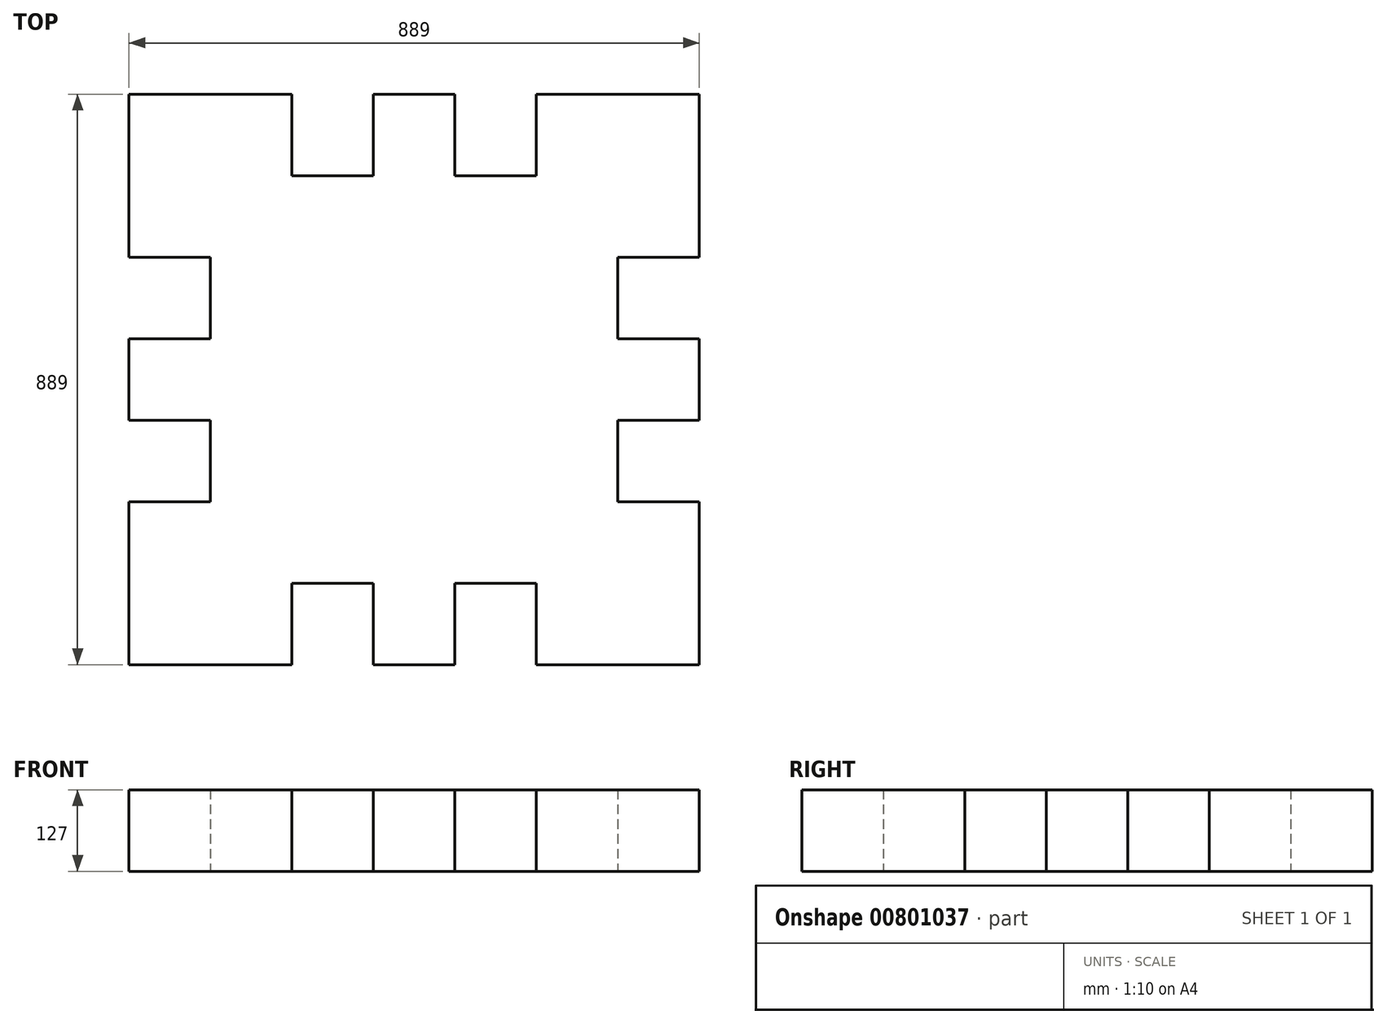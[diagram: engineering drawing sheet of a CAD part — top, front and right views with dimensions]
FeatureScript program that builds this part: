
annotation { "Feature Type Name" : "Feature", "Feature Type Description" : "" }
export const myFeature = defineFeature(function(context is Context, id is Id, definition is map)
    precondition{}
    {
        {
            var Q0;
            Q0=qCreatedBy(makeId("Top.planeOp"),FACE);
            var sketch = newSketch(context, id + "F0", { "sketchPlane" : qUnion([Q0])});
            skLineSegment(sketch, "E0.bottom", {"start": v(0, 0) * mm, "end": v(635, 0) * mm});
            skLineSegment(sketch, "E0.top", {"start": v(0, -635) * mm, "end": v(635, -635) * mm});
            skLineSegment(sketch, "E0.left", {"start": v(0, 0) * mm, "end": v(0, -635) * mm});
            skLineSegment(sketch, "E0.right", {"start": v(635, 0) * mm, "end": v(635, -635) * mm});
            skLineSegment(sketch, "E1.bottom", {"start": v(0, 0) * mm, "end": v(127, 0) * mm});
            skLineSegment(sketch, "E1.top", {"start": v(0, 127) * mm, "end": v(127, 127) * mm});
            skLineSegment(sketch, "E1.left", {"start": v(0, 0) * mm, "end": v(0, 127) * mm});
            skLineSegment(sketch, "E1.right", {"start": v(127, 0) * mm, "end": v(127, 127) * mm});
            skLineSegment(sketch, "E2.bottom", {"start": v(254, 0) * mm, "end": v(381, 0) * mm});
            skLineSegment(sketch, "E2.top", {"start": v(254, 127) * mm, "end": v(381, 127) * mm});
            skLineSegment(sketch, "E2.left", {"start": v(254, 0) * mm, "end": v(254, 127) * mm});
            skLineSegment(sketch, "E2.right", {"start": v(381, 0) * mm, "end": v(381, 127) * mm});
            skLineSegment(sketch, "E3.bottom", {"start": v(635, 0) * mm, "end": v(508, 0) * mm});
            skLineSegment(sketch, "E3.top", {"start": v(635, 127) * mm, "end": v(508, 127) * mm});
            skLineSegment(sketch, "E3.left", {"start": v(635, 0) * mm, "end": v(635, 127) * mm});
            skLineSegment(sketch, "E3.right", {"start": v(508, 0) * mm, "end": v(508, 127) * mm});
            skLineSegment(sketch, "E4.bottom", {"start": v(635, 0) * mm, "end": v(762, 0) * mm});
            skLineSegment(sketch, "E4.top", {"start": v(635, -127) * mm, "end": v(762, -127) * mm});
            skLineSegment(sketch, "E4.left", {"start": v(635, 0) * mm, "end": v(635, -127) * mm});
            skLineSegment(sketch, "E4.right", {"start": v(762, 0) * mm, "end": v(762, -127) * mm});
            skLineSegment(sketch, "E5.bottom", {"start": v(635, -254) * mm, "end": v(762, -254) * mm});
            skLineSegment(sketch, "E5.top", {"start": v(635, -381) * mm, "end": v(762, -381) * mm});
            skLineSegment(sketch, "E5.left", {"start": v(635, -254) * mm, "end": v(635, -381) * mm});
            skLineSegment(sketch, "E5.right", {"start": v(762, -254) * mm, "end": v(762, -381) * mm});
            skLineSegment(sketch, "E6.bottom", {"start": v(635, -635) * mm, "end": v(762, -635) * mm});
            skLineSegment(sketch, "E6.top", {"start": v(635, -508) * mm, "end": v(762, -508) * mm});
            skLineSegment(sketch, "E6.left", {"start": v(635, -635) * mm, "end": v(635, -508) * mm});
            skLineSegment(sketch, "E6.right", {"start": v(762, -635) * mm, "end": v(762, -508) * mm});
            skLineSegment(sketch, "E7.bottom", {"start": v(0, -635) * mm, "end": v(127, -635) * mm});
            skLineSegment(sketch, "E7.top", {"start": v(0, -762) * mm, "end": v(127, -762) * mm});
            skLineSegment(sketch, "E7.left", {"start": v(0, -635) * mm, "end": v(0, -762) * mm});
            skLineSegment(sketch, "E7.right", {"start": v(127, -635) * mm, "end": v(127, -762) * mm});
            skLineSegment(sketch, "E8.bottom", {"start": v(254, -635) * mm, "end": v(381, -635) * mm});
            skLineSegment(sketch, "E8.top", {"start": v(254, -762) * mm, "end": v(381, -762) * mm});
            skLineSegment(sketch, "E8.left", {"start": v(254, -635) * mm, "end": v(254, -762) * mm});
            skLineSegment(sketch, "E8.right", {"start": v(381, -635) * mm, "end": v(381, -762) * mm});
            skLineSegment(sketch, "E9.bottom", {"start": v(635, -635) * mm, "end": v(508, -635) * mm});
            skLineSegment(sketch, "E9.top", {"start": v(635, -762) * mm, "end": v(508, -762) * mm});
            skLineSegment(sketch, "E9.left", {"start": v(635, -635) * mm, "end": v(635, -762) * mm});
            skLineSegment(sketch, "E9.right", {"start": v(508, -635) * mm, "end": v(508, -762) * mm});
            skLineSegment(sketch, "E10.bottom", {"start": v(0, 0) * mm, "end": v(-127, 0) * mm});
            skLineSegment(sketch, "E10.top", {"start": v(0, -127) * mm, "end": v(-127, -127) * mm});
            skLineSegment(sketch, "E10.left", {"start": v(0, 0) * mm, "end": v(0, -127) * mm});
            skLineSegment(sketch, "E10.right", {"start": v(-127, 0) * mm, "end": v(-127, -127) * mm});
            skLineSegment(sketch, "E11.bottom", {"start": v(0, -635) * mm, "end": v(-127, -635) * mm});
            skLineSegment(sketch, "E11.top", {"start": v(0, -508) * mm, "end": v(-127, -508) * mm});
            skLineSegment(sketch, "E11.left", {"start": v(0, -635) * mm, "end": v(0, -508) * mm});
            skLineSegment(sketch, "E11.right", {"start": v(-127, -635) * mm, "end": v(-127, -508) * mm});
            skLineSegment(sketch, "E12.bottom", {"start": v(0, -254) * mm, "end": v(-127, -254) * mm});
            skLineSegment(sketch, "E12.top", {"start": v(0, -381) * mm, "end": v(-127, -381) * mm});
            skLineSegment(sketch, "E12.left", {"start": v(0, -254) * mm, "end": v(0, -381) * mm});
            skLineSegment(sketch, "E12.right", {"start": v(-127, -254) * mm, "end": v(-127, -381) * mm});
            skLineSegment(sketch, "E13.bottom", {"start": v(-127, -635) * mm, "end": v(0, -635) * mm});
            skLineSegment(sketch, "E13.top", {"start": v(-127, -762) * mm, "end": v(0, -762) * mm});
            skLineSegment(sketch, "E13.left", {"start": v(-127, -635) * mm, "end": v(-127, -762) * mm});
            skLineSegment(sketch, "E14.bottom", {"start": v(635, -762) * mm, "end": v(762, -762) * mm});
            skLineSegment(sketch, "E14.left", {"start": v(635, -762) * mm, "end": v(635, -635) * mm});
            skLineSegment(sketch, "E14.right", {"start": v(762, -762) * mm, "end": v(762, -635) * mm});
            skLineSegment(sketch, "E15.bottom", {"start": v(635, 127) * mm, "end": v(762, 127) * mm});
            skLineSegment(sketch, "E15.left", {"start": v(635, 127) * mm, "end": v(635, 0) * mm});
            skLineSegment(sketch, "E15.right", {"start": v(762, 127) * mm, "end": v(762, 0) * mm});
            skLineSegment(sketch, "E16.bottom", {"start": v(-127, 0) * mm, "end": v(0, 0) * mm});
            skLineSegment(sketch, "E16.top", {"start": v(-127, 127) * mm, "end": v(0, 127) * mm});
            skLineSegment(sketch, "E16.left", {"start": v(-127, 0) * mm, "end": v(-127, 127) * mm});
            skSolve(sketch);
        }
        {
            var Q0;
            Q0 = qSketchRegion(id + "F0", true);
            extrude(context, id + "F1", {"entities" : qUnion([Q0]), "depth" : 127 * mm, "offsetDistance" : 25.4 * mm});
        }
    });
